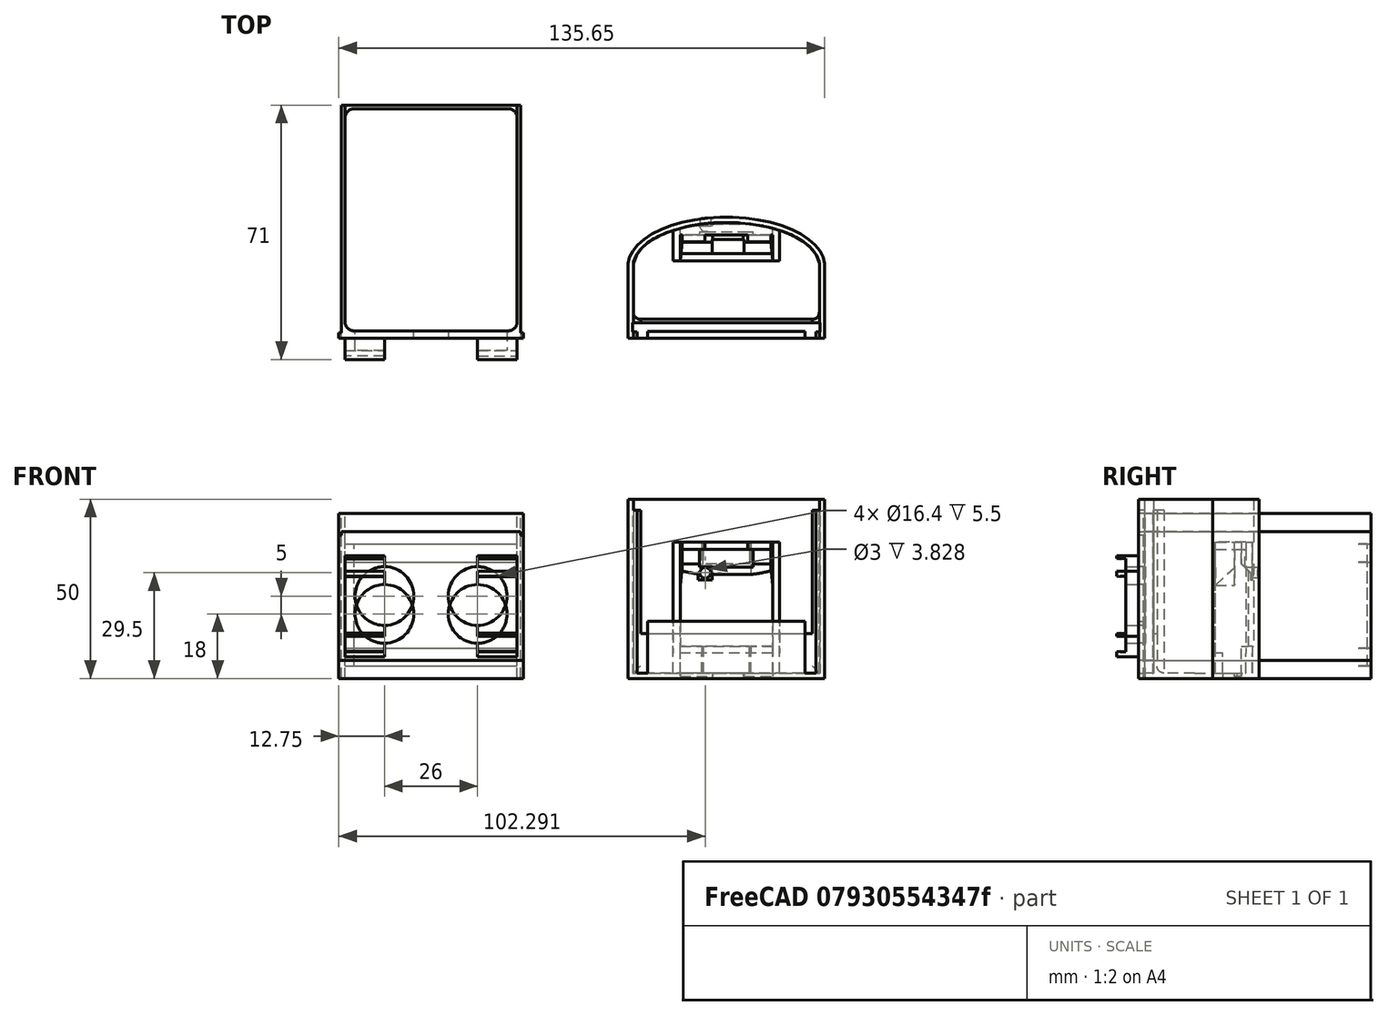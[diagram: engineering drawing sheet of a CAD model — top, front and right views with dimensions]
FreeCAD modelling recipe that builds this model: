
FCSTD DOCUMENT  (FreeCAD 0.18.4R)
Label: sonic.sensor.V4
License: All rights reserved
LicenseURL: http://en.wikipedia.org/wiki/All_rights_reserved
objects: Part::Extrusion×38, Part::Part2DObjectPython×27, Part::Cut×22, Part::Feature×18, Part::MultiFuse×16
note: 121 computed .brp shape members not serialized (recipe doc carries the construction recipe); baked Part::Feature solids carry a one-line shape summary decoded from their .brp

FEATURE [Part::Feature] Slice_child  label="Slice.003"
  Placement = pos=(0,5,0) rot=(0,0,1;0rad)
  shape: bbox 54.92 x 13.01 x 50 mm, 74 faces (baked)
FEATURE [Part::Part2DObjectPython] Rectangle  # Draft 2D object (typed FeaturePython)
  ChamferSize = 0
  Columns = 1
  FilletRadius = 0
  Height = 50
  Length = 54.9181
  MakeFace = true
  Placement = pos=(79.9819,-14.25,-6e-15) rot=(1,0,0;1.5708rad)
  Rows = 1
FEATURE [Part::Extrusion] Extrusion
  Base = -> Rectangle
  Dir = (-1.25e-14,-15.75,-2.1e-14)
  DirMode = 0
  FaceMakerClass = Part::FaceMakerBullseye
  LengthFwd = 0
  LengthRev = 0
  Solid = true
  Symmetric = false
FEATURE [Part::Part2DObjectPython] Rectangle001  # Draft 2D object (typed FeaturePython)
  ChamferSize = 0
  Columns = 1
  FilletRadius = 0
  Height = 48.5
  Length = 51.9024
  MakeFace = true
  Placement = pos=(81.4897,-14.25,1.5) rot=(1,0,0;1.5708rad)
  Rows = 1
FEATURE [Part::Extrusion] Extrusion001
  Base = -> Rectangle001
  Dir = (-1.25e-14,-15.75,-2.1e-14)
  DirMode = 0
  FaceMakerClass = Part::FaceMakerBullseye
  LengthFwd = 0
  LengthRev = 0
  Solid = true
  Symmetric = false
FEATURE [Part::Cut] Cut
  Base = -> Extrusion
  Tool = -> Extrusion001
FEATURE [Part::Part2DObjectPython] Rectangle002  # Draft 2D object (typed FeaturePython)
  ChamferSize = 0
  Columns = 1
  FilletRadius = 0
  Height = 2.5
  Length = 51.9024
  MakeFace = true
  Placement = pos=(81.4897,-25.7833,47) rot=(0,0,1;0rad)
  Rows = 1
FEATURE [Part::Extrusion] Extrusion002
  Base = -> Rectangle002
  Dir = (0,9.1e-14,-45.5)
  DirMode = 0
  FaceMakerClass = Part::FaceMakerBullseye
  LengthFwd = 0
  LengthRev = 0
  Solid = true
  Symmetric = false
FEATURE [Part::Feature] Extrusion004
  Placement = pos=(0,3.6e-15,-3.5) rot=(0,0,1;0rad)
  shape: bbox 47.9 x 2.5 x 34.5 mm, 6 faces (baked)
FEATURE [Part::Cut] Cut001
  Base = -> Extrusion002
  Tool = -> Extrusion004
FEATURE [Part::Feature] Face
  shape: bbox 51.9 x 2e-07 x 45.5 mm, 1 faces, 0 solids (baked)
FEATURE [Part::Extrusion] Extrusion005
  Base = -> Face
  Dir = (0,-1.5,-3e-15)
  DirMode = 0
  FaceMakerClass = Part::FaceMakerBullseye
  LengthFwd = 0
  LengthRev = 0
  Solid = true
  Symmetric = false
FEATURE [Part::Cut] Cut002
  Base = -> Cut001
  Tool = -> Extrusion005
FEATURE [Part::Part2DObjectPython] Rectangle004  # Draft 2D object (typed FeaturePython)
  ChamferSize = 0
  Columns = 1
  FilletRadius = 0
  Height = 14.5
  Length = 43.9024
  MakeFace = true
  Placement = pos=(85.4897,-30,1.5) rot=(1,0,0;1.5708rad)
  Rows = 1
FEATURE [Part::Extrusion] Extrusion006
  Base = -> Rectangle004
  Dir = (-1.38e-14,1.81667,-9.5e-15)
  DirMode = 0
  FaceMakerClass = Part::FaceMakerBullseye
  LengthFwd = 0
  LengthRev = 0
  Solid = true
  Symmetric = false
FEATURE [Part::MultiFuse] Fusion
  Shapes = -> [Cut,Cut002,Extrusion006]
FEATURE [Part::Part2DObjectPython] Rectangle005  # Draft 2D object (typed FeaturePython)
  ChamferSize = 0
  Columns = 1
  FilletRadius = 0
  Height = 1.71667
  Length = 1
  MakeFace = true
  Placement = pos=(132.392,-30,47) rot=(0,0,1;0rad)
  Rows = 1
FEATURE [Part::Extrusion] Extrusion007
  Base = -> Rectangle005
  Dir = (-1.616e-13,1.397e-13,-45.5)
  DirMode = 0
  FaceMakerClass = Part::FaceMakerBullseye
  LengthFwd = 0
  LengthRev = 0
  Solid = true
  Symmetric = false
FEATURE [Part::Part2DObjectPython] Rectangle006  # Draft 2D object (typed FeaturePython)
  ChamferSize = 0
  Columns = 1
  FilletRadius = 0
  Height = 1
  Length = 1.71667
  MakeFace = true
  Placement = pos=(81.4897,-28.2833,47) rot=(0,0,-1;1.5708rad)
  Rows = 1
FEATURE [Part::Extrusion] Extrusion008
  Base = -> Rectangle006
  Dir = (-4.87e-14,1.397e-13,-45.5)
  DirMode = 0
  FaceMakerClass = Part::FaceMakerBullseye
  LengthFwd = 0
  LengthRev = 0
  Solid = true
  Symmetric = false
FEATURE [Part::MultiFuse] Fusion001
  Shapes = -> [Fusion,Extrusion008,Extrusion007]
FEATURE [Part::Part2DObjectPython] Rectangle007  # Draft 2D object (typed FeaturePython)
  ChamferSize = 0
  Columns = 1
  FilletRadius = 0
  Height = 2.5
  Length = 0.2
  MakeFace = true
  Placement = pos=(133.392,-28.2833,50) rot=(0,0,1;0rad)
  Rows = 1
FEATURE [Part::Extrusion] Extrusion009
  Base = -> Rectangle007
  Dir = (0,7.3e-15,-48.5)
  DirMode = 0
  FaceMakerClass = Part::FaceMakerBullseye
  LengthFwd = 0
  LengthRev = 0
  Solid = true
  Symmetric = false
FEATURE [Part::Feature] Extrusion010
  Placement = pos=(-52.1024,4.62e-14,-2.84e-14) rot=(0,0,1;0rad)
  shape: bbox 0.2 x 2.5 x 48.5 mm, 6 faces (baked)
FEATURE [Part::Cut] Cut003
  Base = -> Fusion001
  Tool = -> Extrusion009
FEATURE [Part::Cut] Cut004
  Base = -> Cut003
  Tool = -> Extrusion010
FEATURE [Part::Part2DObjectPython] Rectangle009  # Draft 2D object (typed FeaturePython)
  ChamferSize = 0
  Columns = 1
  FilletRadius = 0
  Height = 2
  Length = 2
  MakeFace = true
  Placement = pos=(133.392,-22.7833,1.5) rot=(0.57735,-0.57735,-0.57735;2.0944rad)
  Rows = 1
FEATURE [Part::Extrusion] Extrusion011
  Base = -> Rectangle009
  Dir = (-51.9024,0,0)
  DirMode = 0
  FaceMakerClass = Part::FaceMakerBullseye
  LengthFwd = 0
  LengthRev = 0
  Solid = true
  Symmetric = false
FEATURE [Part::Part2DObjectPython] Circle  # Draft 2D object (typed FeaturePython)
  FirstAngle = 0
  LastAngle = 0
  MakeFace = true
  Placement = pos=(81.4897,-22.7833,3.5) rot=(0.57735,-0.57735,-0.57735;2.0944rad)
  Radius = 2
  Support = -> [Extrusion011]
FEATURE [Part::Extrusion] Extrusion012
  Base = -> Circle
  Dir = (51.9024,0,0)
  DirMode = 0
  FaceMakerClass = Part::FaceMakerBullseye
  LengthFwd = 0
  LengthRev = 0
  Solid = true
  Symmetric = false
FEATURE [Part::Cut] Cut005
  Base = -> Extrusion011
  Tool = -> Extrusion012
FEATURE [Part::MultiFuse] Fusion002
  Shapes = -> [Cut004,Cut005]
FEATURE [Part::Part2DObjectPython] Rectangle010  # Draft 2D object (typed FeaturePython)
  ChamferSize = 0
  Columns = 1
  FilletRadius = 0
  Height = 2.00245
  Length = 2
  MakeFace = true
  Placement = pos=(133.392,-24.7833,47) rot=(0,0,1;1.5708rad)
  Rows = 1
FEATURE [Part::Extrusion] Extrusion013
  Base = -> Rectangle010
  Dir = (1.161e-13,2.071e-13,-45.5)
  DirMode = 0
  FaceMakerClass = Part::FaceMakerBullseye
  LengthFwd = 0
  LengthRev = 0
  Solid = true
  Symmetric = false
FEATURE [Part::Part2DObjectPython] Circle001  # Draft 2D object (typed FeaturePython)
  FirstAngle = 0
  LastAngle = 0
  MakeFace = true
  Placement = pos=(131.39,-22.7833,47) rot=(0,0,1;1.5708rad)
  Radius = 2
  Support = -> [Extrusion013]
FEATURE [Part::Extrusion] Extrusion014
  Base = -> Circle001
  Dir = (3.53e-14,2.425e-13,-45.5)
  DirMode = 0
  FaceMakerClass = Part::FaceMakerBullseye
  LengthFwd = 0
  LengthRev = 0
  Solid = true
  Symmetric = false
FEATURE [Part::Cut] Cut006
  Base = -> Extrusion013
  Tool = -> Extrusion014
FEATURE [Part::Part2DObjectPython] Rectangle012  # Draft 2D object (typed FeaturePython)
  ChamferSize = 0
  Columns = 1
  FilletRadius = 0
  Height = 2
  Length = 2
  MakeFace = true
  Placement = pos=(83.4897,-24.7833,47) rot=(0,0,1;1.5708rad)
  Rows = 1
  Support = -> [Fusion002]
FEATURE [Part::Extrusion] Extrusion015
  Base = -> Rectangle012
  Dir = (1.161e-13,2.071e-13,-45.5)
  DirMode = 0
  FaceMakerClass = Part::FaceMakerBullseye
  LengthFwd = 0
  LengthRev = 0
  Solid = true
  Symmetric = false
FEATURE [Part::Part2DObjectPython] Circle002  # Draft 2D object (typed FeaturePython)
  FirstAngle = 0
  LastAngle = 0
  MakeFace = true
  Placement = pos=(83.4897,-22.7833,47) rot=(0,0,1;1.5708rad)
  Radius = 2
  Support = -> [Extrusion015]
FEATURE [Part::Extrusion] Extrusion016
  Base = -> Circle002
  Dir = (3.53e-14,2.425e-13,-45.5)
  DirMode = 0
  FaceMakerClass = Part::FaceMakerBullseye
  LengthFwd = 0
  LengthRev = 0
  Solid = true
  Symmetric = false
FEATURE [Part::Cut] Cut007
  Base = -> Extrusion015
  Tool = -> Extrusion016
FEATURE [Part::MultiFuse] Fusion003
  Shapes = -> [Cut007,Fusion002,Cut006]
FEATURE [Part::Feature] Face001
  shape: bbox 54.92 x 2e-07 x 50 mm, 1 faces, 0 solids (baked)
FEATURE [Part::Extrusion] Extrusion017
  Base = -> Face001
  Dir = (4e-15,5,6.7e-15)
  DirMode = 0
  FaceMakerClass = Part::FaceMakerBullseye
  LengthFwd = 0
  LengthRev = 0
  Solid = true
  Symmetric = false
FEATURE [Part::MultiFuse] Fusion004
  Shapes = -> [Fusion003,Extrusion017,Slice_child]
FEATURE [Part::Cut] Cut029
FEATURE [Part::Part2DObjectPython] Rectangle013  # Draft 2D object (typed FeaturePython)
  ChamferSize = 0
  Columns = 1
  FilletRadius = 0
  Height = 1.5
  Length = 48
  MakeFace = true
  Placement = pos=(49,-33.5,33.5001) rot=(0,0,1;3.14159rad)
  Rows = 1
  Support = -> [Cut029]
FEATURE [Part::Extrusion] Extrusion018
  Base = -> Rectangle013
  Dir = (0,0,0.699902)
  DirMode = 0
  FaceMakerClass = Part::FaceMakerBullseye
  LengthFwd = 0
  LengthRev = 0
  Solid = true
  Symmetric = false
FEATURE [Part::Part2DObjectPython] Rectangle014  # Draft 2D object (typed FeaturePython)
  ChamferSize = 0
  Columns = 1
  FilletRadius = 0
  Height = 1.5
  Length = 48
  MakeFace = true
  Placement = pos=(1,-33.5,12.5001) rot=(1,0,0;3.14159rad)
  Rows = 1
FEATURE [Part::Extrusion] Extrusion019
  Base = -> Rectangle014
  Dir = (0,0,-0.699902)
  DirMode = 0
  FaceMakerClass = Part::FaceMakerBullseye
  LengthFwd = 0
  LengthRev = 0
  Solid = true
  Symmetric = false
FEATURE [Part::Part2DObjectPython] Rectangle015  # Draft 2D object (typed FeaturePython)
  ChamferSize = 0
  Columns = 1
  FilletRadius = 0
  Height = 22.3998
  Length = 26
  MakeFace = true
  Placement = pos=(12,-33.5,11.8002) rot=(1,0,0;1.5708rad)
  Rows = 1
  Support = -> [Cut029]
FEATURE [Part::Extrusion] Extrusion020
  Base = -> Rectangle015
  Dir = (-6e-16,-19.5709,4.3e-15)
  DirMode = 0
  FaceMakerClass = Part::FaceMakerBullseye
  LengthFwd = 0
  LengthRev = 0
  Solid = true
  Symmetric = false
FEATURE [Part::MultiFuse] Fusion005
  Shapes = -> [Extrusion018,Extrusion019]
FEATURE [Part::Cut] Cut030
  Base = -> Fusion005
  Tool = -> Extrusion020
FEATURE [Part::Part2DObjectPython] Rectangle017  # Draft 2D object (typed FeaturePython)
  ChamferSize = 0
  Columns = 1
  FilletRadius = 0
  Height = 0.699902
  Length = 1
  MakeFace = true
  Placement = pos=(1,-35,33.5001) rot=(0.57735,-0.57735,-0.57735;2.0944rad)
  Rows = 1
FEATURE [Part::Extrusion] Extrusion021
  Base = -> Rectangle017
  Dir = (11,0,0)
  DirMode = 0
  FaceMakerClass = Part::FaceMakerBullseye
  LengthFwd = 0
  LengthRev = 0
  Solid = true
  Symmetric = false
FEATURE [Part::Part2DObjectPython] Wire  # Draft 2D object (typed FeaturePython)
  ChamferSize = 0
  Closed = true
  End = (1,-35,33.5001)
  FilletRadius = 0
  Length = 2.10499
  MakeFace = true
  Placement = pos=(1,-36,33.5001) rot=(0.57735,-0.57735,-0.57735;2.0944rad)
  Points = (3) [(0,0,0),(-1,-0.1,-1.77636e-15),(-1,0,0)]
  Start = (1,-36,33.5001)
  Subdivisions = 0
  Support = -> [Extrusion021]
FEATURE [Part::Extrusion] Extrusion022
  Base = -> Wire
  Dir = (11,0,1.954e-13)
  DirMode = 0
  FaceMakerClass = Part::FaceMakerBullseye
  LengthFwd = 0
  LengthRev = 0
  Solid = true
  Symmetric = false
FEATURE [Part::MultiFuse] Fusion006
  Shapes = -> [Extrusion021,Extrusion022]
FEATURE [Part::Feature] Fusion007
  Placement = pos=(37,0,0) rot=(0,0,1;0rad)
  shape: bbox 11 x 1 x 0.7999 mm, 9 faces (baked)
FEATURE [Part::Part2DObjectPython] Rectangle018  # Draft 2D object (typed FeaturePython)
  ChamferSize = 0
  Columns = 1
  FilletRadius = 0
  Height = 0.699902
  Length = 1
  MakeFace = true
  Placement = pos=(1,-36,12.5001) rot=(0.57735,0.57735,-0.57735;4.18879rad)
  Rows = 1
FEATURE [Part::Extrusion] Extrusion023
  Base = -> Rectangle018
  Dir = (11,0,0)
  DirMode = 0
  FaceMakerClass = Part::FaceMakerBullseye
  LengthFwd = 0
  LengthRev = 0
  Solid = true
  Symmetric = false
FEATURE [Part::Part2DObjectPython] Wire001  # Draft 2D object (typed FeaturePython)
  ChamferSize = 0
  Closed = true
  End = (1,-35,12.6001)
  FilletRadius = 0
  Length = 2.10499
  MakeFace = true
  Placement = pos=(1,-35,12.5001) rot=(0.57735,0.57735,-0.57735;4.18879rad)
  Points = (3) [(0,0,0),(-1,0,0),(0,-0.1,0)]
  Start = (1,-35,12.5001)
  Subdivisions = 0
FEATURE [Part::Extrusion] Extrusion024
  Base = -> Wire001
  Dir = (11,0,0)
  DirMode = 0
  FaceMakerClass = Part::FaceMakerBullseye
  LengthFwd = 0
  LengthRev = 0
  Solid = true
  Symmetric = false
FEATURE [Part::MultiFuse] Fusion008
  Shapes = -> [Extrusion023,Extrusion024]
FEATURE [Part::Feature] Fusion009
  Placement = pos=(37,0,0) rot=(0,0,1;0rad)
  shape: bbox 11 x 1 x 0.7999 mm, 9 faces (baked)
FEATURE [Part::MultiFuse] Fusion010
  Shapes = -> [Cut030,Fusion007]
FEATURE [Part::MultiFuse] Fusion011
  Shapes = -> [Fusion010,Fusion009]
FEATURE [Part::MultiFuse] Fusion012
  Shapes = -> [Fusion011,Fusion006]
FEATURE [Part::MultiFuse] Fusion013
  Shapes = -> [Fusion012,Fusion008]
FEATURE [Part::MultiFuse] Fusion014
  Shapes = -> [Fusion013]
FEATURE [Part::MultiFuse] Fusion015
  Shapes = -> [Cut029,Fusion014]
FEATURE [Part::Feature] Fusion016
  Placement = pos=(3.6e-15,0,-5) rot=(0,0,1;0rad)
  shape: bbox 51.5 x 71 x 41 mm, 89 faces (baked)
FEATURE [Part::Part2DObjectPython] Rectangle019  # Draft 2D object (typed FeaturePython)
  ChamferSize = 0
  Columns = 1
  FilletRadius = 0
  Height = 6
  Length = 11
  MakeFace = true
  Placement = pos=(38,-30,6.8002) rot=(1,0,0;3.14159rad)
  Rows = 1
  Support = -> [Fusion016]
FEATURE [Part::Extrusion] Extrusion025
  Base = -> Rectangle019
  Dir = (0,0,-0.699902)
  DirMode = 0
  FaceMakerClass = Part::FaceMakerBullseye
  LengthFwd = 0
  LengthRev = 0
  Solid = true
  Symmetric = false
FEATURE [Part::Part2DObjectPython] Rectangle020  # Draft 2D object (typed FeaturePython)
  ChamferSize = 0
  Columns = 1
  FilletRadius = 0
  Height = 11
  Length = 6
  MakeFace = true
  Placement = pos=(12,-30,6.8002) rot=(0.707107,-0.707107,0;3.14159rad)
  Rows = 1
  Support = -> [Fusion016]
FEATURE [Part::Extrusion] Extrusion026
  Base = -> Rectangle020
  Dir = (0,0,-0.699902)
  DirMode = 0
  FaceMakerClass = Part::FaceMakerBullseye
  LengthFwd = 0
  LengthRev = 0
  Solid = true
  Symmetric = false
FEATURE [Part::Part2DObjectPython] Rectangle021  # Draft 2D object (typed FeaturePython)
  ChamferSize = 0
  Columns = 1
  FilletRadius = 0
  Height = 6
  Length = 11
  MakeFace = true
  Placement = pos=(49,-30,29.2) rot=(0,0,1;3.14159rad)
  Rows = 1
  Support = -> [Fusion016]
FEATURE [Part::Part2DObjectPython] Rectangle022  # Draft 2D object (typed FeaturePython)
  ChamferSize = 0
  Columns = 1
  FilletRadius = 0
  Height = 6
  Length = 11
  MakeFace = true
  Placement = pos=(12,-30,29.2) rot=(0,0,1;3.14159rad)
  Rows = 1
FEATURE [Part::Extrusion] Extrusion027
  Base = -> Rectangle022
  Dir = (0,0,0.699902)
  DirMode = 0
  FaceMakerClass = Part::FaceMakerBullseye
  LengthFwd = 0
  LengthRev = 0
  Solid = true
  Symmetric = false
FEATURE [Part::Extrusion] Extrusion028
  Base = -> Rectangle021
  Dir = (0,0,0.749176)
  DirMode = 0
  FaceMakerClass = Part::FaceMakerBullseye
  LengthFwd = 0
  LengthRev = 0
  Solid = true
  Symmetric = false
FEATURE [Part::MultiFuse] Fusion017
  Shapes = -> [Extrusion026,Extrusion025,Extrusion028,Extrusion027]
FEATURE [Part::MultiFuse] Fusion018
  Shapes = -> [Fusion016,Fusion017]
FEATURE [Part::Feature] Face002
  Placement = pos=(0,5,0) rot=(0,0,1;0rad)
  shape: bbox 1.002e-05 x 1.2 x 0.75 mm, 1 faces, 0 solids (baked)
FEATURE [Part::Extrusion] Extrusion029
  Base = -> Face002
  Dir = (0.2,0,0)
  DirMode = 0
  FaceMakerClass = Part::FaceMakerBullseye
  LengthFwd = 0
  LengthRev = 0
  Solid = true
  Symmetric = false
FEATURE [Part::Cut] Cut031
  Base = -> Fusion004
  Tool = -> Extrusion029
FEATURE [Part::Feature] Face003
  Placement = pos=(0,5,0) rot=(0,0,1;0rad)
  shape: bbox 1.002e-05 x 1.2 x 0.75 mm, 1 faces, 0 solids (baked)
FEATURE [Part::Extrusion] Extrusion030
  Base = -> Face003
  Dir = (-0.2,0,0)
  DirMode = 0
  FaceMakerClass = Part::FaceMakerBullseye
  LengthFwd = 0
  LengthRev = 0
  Solid = true
  Symmetric = false
FEATURE [Part::Cut] Cut032
  Base = -> Cut031
  Tool = -> Extrusion030
FEATURE [Part::Feature] Face004
  shape: bbox 8.9 x 1.8 x 1.002e-05 mm, 1 faces, 0 solids (baked)
FEATURE [Part::Extrusion] Extrusion031
  Base = -> Face004
  Dir = (0,0,-0.2)
  DirMode = 0
  FaceMakerClass = Part::FaceMakerBullseye
  LengthFwd = 0
  LengthRev = 0
  Solid = true
  Symmetric = false
FEATURE [Part::Cut] Cut033
  Base = -> Cut032
  Tool = -> Extrusion031
FEATURE [Part::Feature] Face005
  shape: bbox 0.2 x 1.2 x 1.002e-05 mm, 1 faces, 0 solids (baked)
FEATURE [Part::Extrusion] Extrusion032
  Base = -> Face005
  Dir = (0,0,-0.2)
  DirMode = 0
  FaceMakerClass = Part::FaceMakerBullseye
  LengthFwd = 0
  LengthRev = 0
  Solid = true
  Symmetric = false
FEATURE [Part::Cut] Cut034
  Base = -> Cut033
  Tool = -> Extrusion032
FEATURE [Part::Feature] Face006
  shape: bbox 8 x 1.8 x 1.002e-05 mm, 1 faces, 0 solids (baked)
FEATURE [Part::Extrusion] Extrusion033
  Base = -> Face006
  Dir = (0,0,-0.2)
  DirMode = 0
  FaceMakerClass = Part::FaceMakerBullseye
  LengthFwd = 0
  LengthRev = 0
  Solid = true
  Symmetric = false
FEATURE [Part::Cut] Cut035
  Base = -> Cut034
  Tool = -> Extrusion033
FEATURE [Part::Feature] Face007
  shape: bbox 0.2 x 1.2 x 1.002e-05 mm, 1 faces, 0 solids (baked)
FEATURE [Part::Extrusion] Extrusion034
  Base = -> Face007
  Dir = (0,0,-0.2)
  DirMode = 0
  FaceMakerClass = Part::FaceMakerBullseye
  LengthFwd = 0
  LengthRev = 0
  Solid = true
  Symmetric = false
FEATURE [Part::Cut] Cut036
  Base = -> Cut035
  Tool = -> Extrusion034
FEATURE [Part::Feature] Face008
  shape: bbox 8 x 1.002e-05 x 0.75 mm, 1 faces, 0 solids (baked)
FEATURE [Part::Extrusion] Extrusion035
  Base = -> Face008
  Dir = (0,-0.2,0)
  DirMode = 0
  FaceMakerClass = Part::FaceMakerBullseye
  LengthFwd = 0
  LengthRev = 0
  Solid = true
  Symmetric = false
FEATURE [Part::Feature] Face009
  shape: bbox 8 x 1.002e-05 x 0.2 mm, 1 faces, 0 solids (baked)
FEATURE [Part::Extrusion] Extrusion036
  Base = -> Face009
  Dir = (0,-0.2,0)
  DirMode = 0
  FaceMakerClass = Part::FaceMakerBullseye
  LengthFwd = 0
  LengthRev = 0
  Solid = true
  Symmetric = false
FEATURE [Part::Cut] Cut037
  Base = -> Cut036
  Tool = -> Extrusion035
FEATURE [Part::Cut] Cut038
  Base = -> Cut037
  Tool = -> Extrusion036
FEATURE [Part::Feature] Face010
  shape: bbox 8.9 x 1.002e-05 x 0.75 mm, 1 faces, 0 solids (baked)
FEATURE [Part::Extrusion] Extrusion037
  Base = -> Face010
  Dir = (0,-0.2,0)
  DirMode = 0
  FaceMakerClass = Part::FaceMakerBullseye
  LengthFwd = 0
  LengthRev = 0
  Solid = true
  Symmetric = false
FEATURE [Part::Feature] Face011
  shape: bbox 8.9 x 1.002e-05 x 0.2 mm, 1 faces, 0 solids (baked)
FEATURE [Part::Extrusion] Extrusion038
  Base = -> Face011
  Dir = (0,-0.2,0)
  DirMode = 0
  FaceMakerClass = Part::FaceMakerBullseye
  LengthFwd = 0
  LengthRev = 0
  Solid = true
  Symmetric = false
FEATURE [Part::Cut] Cut039
  Base = -> Cut038
  Tool = -> Extrusion037
FEATURE [Part::Cut] Cut040
  Base = -> Cut039
  Tool = -> Extrusion038
FEATURE [Part::Part2DObjectPython] Rectangle023  # Draft 2D object (typed FeaturePython)
  ChamferSize = 0
  Columns = 1
  FilletRadius = 0
  Height = 1.5
  Length = 0.75
  MakeFace = true
  Placement = pos=(-0.75,-30,41) rot=(0,0,1;0rad)
  Rows = 1
  Support = -> [Fusion018]
FEATURE [Part::Part2DObjectPython] Rectangle024  # Draft 2D object (typed FeaturePython)
  ChamferSize = 0
  Columns = 1
  FilletRadius = 0
  Height = 1.5
  Length = 0.75
  MakeFace = true
  Placement = pos=(50,-30,41) rot=(0,0,1;0rad)
  Rows = 1
FEATURE [Part::Extrusion] Extrusion039
  Base = -> Rectangle024
  Dir = (0,0,-1)
  DirMode = 0
  FaceMakerClass = Part::FaceMakerBullseye
  LengthFwd = 0
  LengthRev = 0
  Solid = true
  Symmetric = false
FEATURE [Part::Extrusion] Extrusion040
  Base = -> Rectangle023
  Dir = (0,0,-1)
  DirMode = 0
  FaceMakerClass = Part::FaceMakerBullseye
  LengthFwd = 0
  LengthRev = 0
  Solid = true
  Symmetric = false
FEATURE [Part::Cut] Cut041
  Base = -> Fusion018
  Tool = -> Extrusion039
FEATURE [Part::Cut] Cut042
  Base = -> Cut041
  Tool = -> Extrusion040
FEATURE [Part::Part2DObjectPython] Line  # Draft 2D object (typed FeaturePython)
  ChamferSize = 0
  Closed = false
  End = (134.9,-22.125,42)
  FilletRadius = 0
  Length = 8
  MakeFace = true
  Placement = pos=(134.9,-22.125,50) rot=(0.57735,0.57735,0.57735;2.0944rad)
  Points = (2) [(0,0,0),(0,-8,0)]
  Start = (134.9,-22.125,50)
  Subdivisions = 0
  Support = -> [Cut040]
